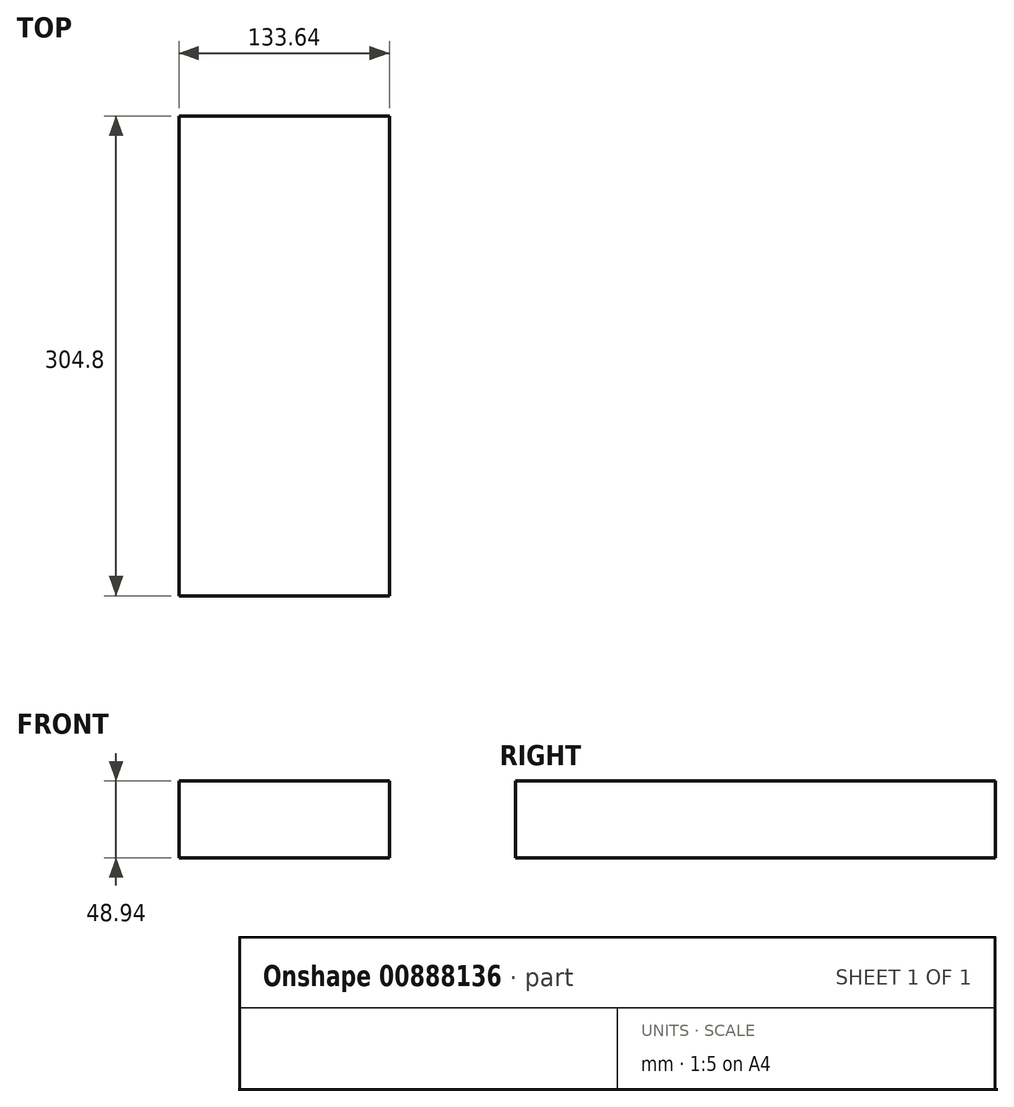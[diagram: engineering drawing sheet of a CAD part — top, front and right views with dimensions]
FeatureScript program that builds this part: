
annotation { "Feature Type Name" : "Feature", "Feature Type Description" : "" }
export const myFeature = defineFeature(function(context is Context, id is Id, definition is map)
    precondition{}
    {
        {
            var Q0;
            Q0=qCreatedBy(makeId("Front.planeOp"),FACE);
            var sketch = newSketch(context, id + "F0", { "sketchPlane" : qUnion([Q0])});
            skLineSegment(sketch, "E0.bottom", {"start": v(-66.82, 24.47) * mm, "end": v(66.82, 24.47) * mm});
            skLineSegment(sketch, "E0.top", {"start": v(-66.82, -24.47) * mm, "end": v(66.82, -24.47) * mm});
            skLineSegment(sketch, "E0.left", {"start": v(-66.82, 24.47) * mm, "end": v(-66.82, -24.47) * mm});
            skLineSegment(sketch, "E0.right", {"start": v(66.82, 24.47) * mm, "end": v(66.82, -24.47) * mm});
            skPoint(sketch, "E0.middle", {"position": v(0, 0) * mm});
            skSolve(sketch);
        }
        {
            var Q0;
            Q0=makeQuery(id+"F0.imprint","IMPRINT",FACE,{"disambiguationData":[TD([[makeQuery(id+"F0.imprint","IMPRINT",EDGE,{"derivedFrom":sQuery(id+"F0.wireOp",EDGE,"E0.bottom")}),-1.0]])]});
            extrude(context, id + "F1", {"entities" : qUnion([Q0]), "depth" : 304.8 * mm, "offsetDistance" : 25.4 * mm});
        }
    });
